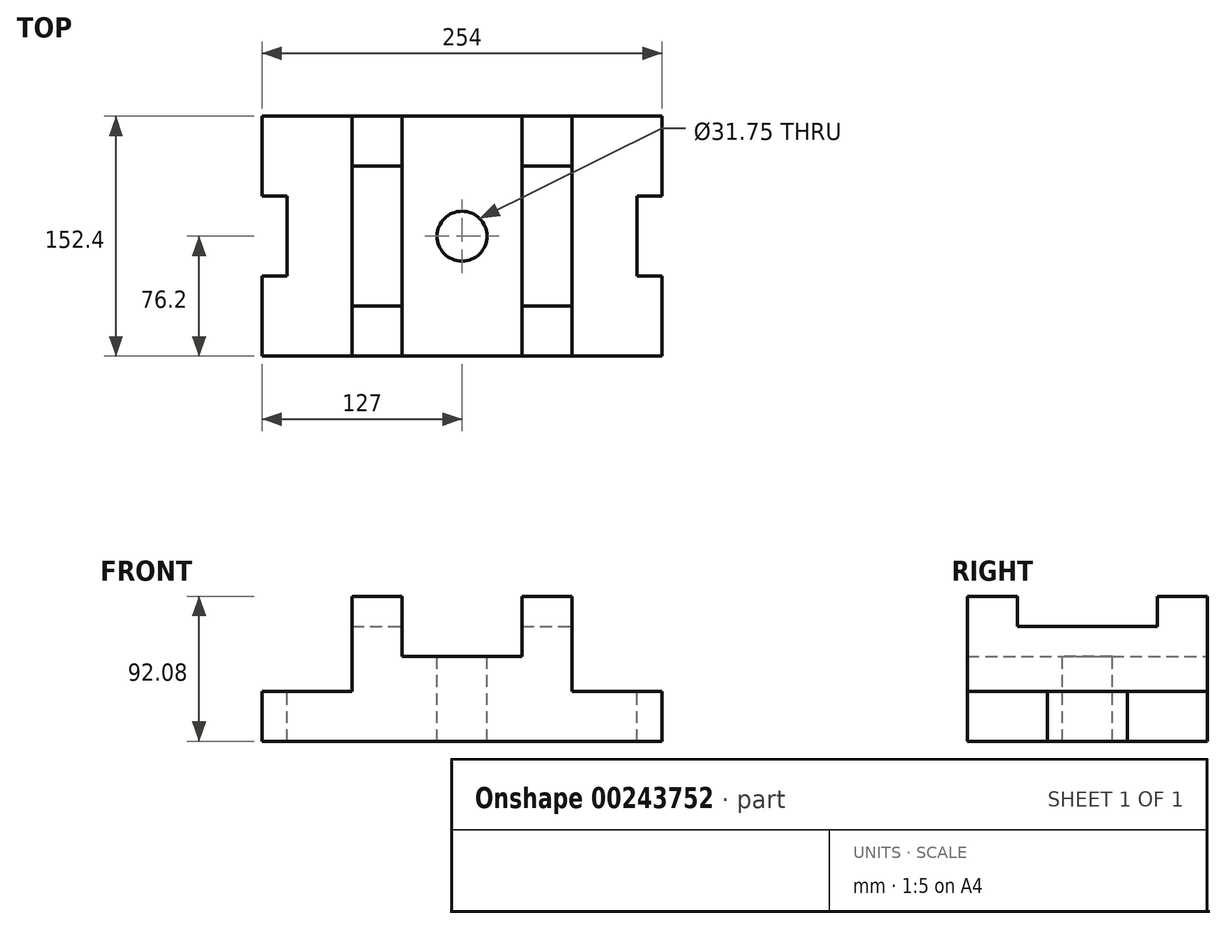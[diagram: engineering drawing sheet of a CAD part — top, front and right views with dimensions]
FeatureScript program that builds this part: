
annotation { "Feature Type Name" : "Feature", "Feature Type Description" : "" }
export const myFeature = defineFeature(function(context is Context, id is Id, definition is map)
    precondition{}
    {
        {
            var Q0;
            Q0=qCreatedBy(makeId("Front.planeOp"),FACE);
            var sketch = newSketch(context, id + "F0", { "sketchPlane" : qUnion([Q0])});
            skLineSegment(sketch, "E0.bottom", {"start": v(0, 0) * mm, "end": v(-254, 0) * mm});
            skLineSegment(sketch, "E0.left", {"start": v(0, 0) * mm, "end": v(0, 31.75) * mm});
            skLineSegment(sketch, "E0.right", {"start": v(-254, 0) * mm, "end": v(-254, 31.75) * mm});
            skLineSegment(sketch, "E1", {"start": v(0, 31.75) * mm, "end": v(-57.15, 31.75) * mm});
            skLineSegment(sketch, "E2", {"start": v(-254, 31.75) * mm, "end": v(-196.85, 31.75) * mm});
            skLineSegment(sketch, "E3", {"start": v(-57.15, 31.75) * mm, "end": v(-57.15, 92.07) * mm});
            skLineSegment(sketch, "E4", {"start": v(-57.15, 92.07) * mm, "end": v(-88.9, 92.07) * mm});
            skLineSegment(sketch, "E5", {"start": v(-88.9, 92.07) * mm, "end": v(-88.9, 73.02) * mm});
            skLineSegment(sketch, "E6", {"start": v(-254, 0) * mm, "end": v(-127, 0) * mm});
            skLineSegment(sketch, "E7.MirrorCS", {"start": v(-165.1, 92.07) * mm, "end": v(-165.1, 73.02) * mm});
            skLineSegment(sketch, "E8.MirrorCS", {"start": v(-196.85, 92.07) * mm, "end": v(-165.1, 92.07) * mm});
            skLineSegment(sketch, "E9.MirrorCS", {"start": v(-196.85, 31.75) * mm, "end": v(-196.85, 92.07) * mm});
            skLineSegment(sketch, "E10", {"start": v(-88.9, 73.02) * mm, "end": v(-165.1, 73.02) * mm});
            skSolve(sketch);
        }
        {
            var Q0;
            Q0=makeQuery(id+"F0.imprint","IMPRINT",FACE,{"disambiguationData":[TD([[makeQuery(id+"F0.imprint","IMPRINT",EDGE,{"derivedFrom":sQuery(id+"F0.wireOp",EDGE,"E0.bottom")}),-1.0]])]});
            extrude(context, id + "F1", {"entities" : qUnion([Q0]), "depth" : 152.4 * mm});
        }
        {
            var Q0;
            Q0=makeQuery(id+"F1.opExtrude","SWEPT_FACE",FACE,{"disambiguationData":[OSD([sQuery(id+"F0.wireOp",EDGE,"E1")])]});
            var sketch = newSketch(context, id + "F2", { "sketchPlane" : qUnion([Q0])});
            skLineSegment(sketch, "E11", {"start": v(0, -152.4) * mm, "end": v(0, -101.6) * mm});
            skLineSegment(sketch, "E12", {"start": v(0, 0) * mm, "end": v(0, -50.8) * mm});
            skLineSegment(sketch, "E13", {"start": v(0, -50.8) * mm, "end": v(-15.87, -50.8) * mm});
            skLineSegment(sketch, "E14", {"start": v(0, -101.6) * mm, "end": v(-15.88, -101.6) * mm});
            skLineSegment(sketch, "E15", {"start": v(-15.87, -50.8) * mm, "end": v(-15.88, -101.6) * mm});
            skSolve(sketch);
        }
        {
            var Q0;
            {var subQ0=sQuery(id+"F2.wireOp",EDGE,"E13");Q0=makeQuery(id+"F2.imprint","IMPRINT",FACE,{"disambiguationData":[TD([[makeQuery(id+"F2.imprint","IMPRINT",EDGE,{"derivedFrom":subQ0}),1.0]])]});}
            extrude(context, id + "F3", {"entities" : qUnion([Q0]), "operationType" : NewBodyOperationType.REMOVE, "endBound" : BoundingType.THROUGH_ALL, "oppositeDirection" : true, "depth" : 25.4 * mm});
        }
        {
            var Q0;
            Q0=makeQuery(id+"F1.opExtrude","SWEPT_FACE",FACE,{"disambiguationData":[OSD([sQuery(id+"F0.wireOp",EDGE,"E2")])]});
            var sketch = newSketch(context, id + "F4", { "sketchPlane" : qUnion([Q0])});
            skLineSegment(sketch, "E16", {"start": v(-254, -152.4) * mm, "end": v(-254, -101.6) * mm});
            skLineSegment(sketch, "E17", {"start": v(-254, -101.6) * mm, "end": v(-254, -50.8) * mm});
            skLineSegment(sketch, "E18", {"start": v(-254, -50.8) * mm, "end": v(-254, 0) * mm});
            skLineSegment(sketch, "E19", {"start": v(-254, -101.6) * mm, "end": v(-238.12, -101.6) * mm});
            skLineSegment(sketch, "E20", {"start": v(-238.12, -101.6) * mm, "end": v(-238.12, -50.8) * mm});
            skLineSegment(sketch, "E21", {"start": v(-254, -50.8) * mm, "end": v(-238.12, -50.8) * mm});
            skLineSegment(sketch, "E22", {"start": v(-254, -50.8) * mm, "end": v(-254, -101.6) * mm});
            skSolve(sketch);
        }
        {
            var Q0;
            Q0=makeQuery(id+"F4.imprint","IMPRINT",FACE,{"disambiguationData":[TD([[makeQuery(id+"F4.imprint","IMPRINT",EDGE,{"derivedFrom":sQuery(id+"F4.wireOp",EDGE,"E19")}),1.0]])]});
            extrude(context, id + "F5", {"entities" : qUnion([Q0]), "operationType" : NewBodyOperationType.REMOVE, "endBound" : BoundingType.THROUGH_ALL, "oppositeDirection" : true, "depth" : 25.4 * mm});
        }
        {
            var Q0;
            Q0=makeQuery(id+"F1.opExtrude","SWEPT_FACE",FACE,{"disambiguationData":[OSD([sQuery(id+"F0.wireOp",EDGE,"E10")])]});
            var sketch = newSketch(context, id + "F6", { "sketchPlane" : qUnion([Q0])});
            skSolve(sketch);
        }
        {
            var Q0;
            {var subQ0=sQuery(id+"F0.wireOp",EDGE,"E10");Q0=makeQuery(id+"F6.imprint","IMPRINT",FACE,{"disambiguationData":[TD([[makeQuery(id+"F6.imprint","IMPRINT",EDGE,{"derivedFrom":makeQuery(id+"F1.opExtrude","CAP_EDGE",EDGE,{"disambiguationData":[OSD([subQ0])],"isStart":true})}),1.0]])]});}
            extrude(context, id + "F7", {"entities" : qUnion([Q0]), "operationType" : NewBodyOperationType.REMOVE, "oppositeDirection" : true, "depth" : 19.05 * mm});
        }
        {
            var Q0;
            Q0=makeQuery(id+"F1.opExtrude","SWEPT_FACE",FACE,{"disambiguationData":[OSD([sQuery(id+"F0.wireOp",EDGE,"E8.MirrorCS")])]});
            var sketch = newSketch(context, id + "F8", { "sketchPlane" : qUnion([Q0])});
            skLineSegment(sketch, "E23.bottom", {"start": v(-196.85, 0) * mm, "end": v(-165.1, 0) * mm});
            skLineSegment(sketch, "E23.top", {"start": v(-196.85, -31.75) * mm, "end": v(-165.1, -31.75) * mm});
            skLineSegment(sketch, "E23.left", {"start": v(-196.85, 0) * mm, "end": v(-196.85, -31.75) * mm});
            skLineSegment(sketch, "E23.right", {"start": v(-165.1, 0) * mm, "end": v(-165.1, -31.75) * mm});
            skLineSegment(sketch, "E24.bottom", {"start": v(-196.85, -152.4) * mm, "end": v(-165.1, -152.4) * mm});
            skLineSegment(sketch, "E24.top", {"start": v(-196.85, -120.65) * mm, "end": v(-165.1, -120.65) * mm});
            skLineSegment(sketch, "E24.left", {"start": v(-196.85, -152.4) * mm, "end": v(-196.85, -120.65) * mm});
            skLineSegment(sketch, "E24.right", {"start": v(-165.1, -152.4) * mm, "end": v(-165.1, -120.65) * mm});
            skLineSegment(sketch, "E25.left", {"start": v(-196.85, -120.65) * mm, "end": v(-196.85, -31.75) * mm});
            skLineSegment(sketch, "E25.right", {"start": v(-165.1, -120.65) * mm, "end": v(-165.1, -31.75) * mm});
            skSolve(sketch);
        }
        {
            var Q0;
            Q0=makeQuery(id+"F1.opExtrude","SWEPT_FACE",FACE,{"disambiguationData":[OSD([sQuery(id+"F0.wireOp",EDGE,"E4")])]});
            var sketch = newSketch(context, id + "F9", { "sketchPlane" : qUnion([Q0])});
            skLineSegment(sketch, "E26.bottom", {"start": v(-88.9, 0) * mm, "end": v(-57.15, 0) * mm});
            skLineSegment(sketch, "E26.top", {"start": v(-88.9, -31.75) * mm, "end": v(-57.15, -31.75) * mm});
            skLineSegment(sketch, "E26.left", {"start": v(-88.9, 0) * mm, "end": v(-88.9, -31.75) * mm});
            skLineSegment(sketch, "E26.right", {"start": v(-57.15, 0) * mm, "end": v(-57.15, -31.75) * mm});
            skLineSegment(sketch, "E27.bottom", {"start": v(-88.9, -152.4) * mm, "end": v(-57.15, -152.4) * mm});
            skLineSegment(sketch, "E27.top", {"start": v(-88.9, -120.65) * mm, "end": v(-57.15, -120.65) * mm});
            skLineSegment(sketch, "E27.left", {"start": v(-88.9, -152.4) * mm, "end": v(-88.9, -120.65) * mm});
            skLineSegment(sketch, "E27.right", {"start": v(-57.15, -152.4) * mm, "end": v(-57.15, -120.65) * mm});
            skLineSegment(sketch, "E28.left", {"start": v(-88.9, -120.65) * mm, "end": v(-88.9, -31.75) * mm});
            skLineSegment(sketch, "E28.right", {"start": v(-57.15, -120.65) * mm, "end": v(-57.15, -31.75) * mm});
            skSolve(sketch);
        }
        {
            var Q0;
            Q0=makeQuery(id+"F9.imprint","IMPRINT",FACE,{"disambiguationData":[TD([[makeQuery(id+"F9.imprint","IMPRINT",EDGE,{"derivedFrom":sQuery(id+"F9.wireOp",EDGE,"E27.top")}),1.0]])]});
            extrude(context, id + "F10", {"entities" : qUnion([Q0]), "operationType" : NewBodyOperationType.REMOVE, "oppositeDirection" : true, "depth" : 19.05 * mm});
        }
        {
            var Q0;
            Q0=makeQuery(id+"F8.imprint","IMPRINT",FACE,{"disambiguationData":[TD([[makeQuery(id+"F8.imprint","IMPRINT",EDGE,{"derivedFrom":sQuery(id+"F8.wireOp",EDGE,"E24.top")}),1.0]])]});
            extrude(context, id + "F11", {"entities" : qUnion([Q0]), "operationType" : NewBodyOperationType.REMOVE, "oppositeDirection" : true, "depth" : 19.05 * mm});
        }
        {
            var Q0;
            Q0=makeQuery(id+"F7.boolean.opBoolean","COPY",FACE,{"derivedFrom":makeQuery(id+"F7.opExtrude","CAP_FACE",FACE,{"disambiguationData":[OSD([sQuery(id+"F0.wireOp",EDGE,"E5"),sQuery(id+"F0.wireOp",EDGE,"E10"),sQuery(id+"F0.wireOp",EDGE,"E7.MirrorCS")])],"isStart":false})});
            var sketch = newSketch(context, id + "F12", { "sketchPlane" : qUnion([Q0])});
            skCircle(sketch, "E29", {"center": v(-127, -76.2) * mm, "radius": 15.88 * mm});
            skSolve(sketch);
        }
        {
            var Q0;
            Q0=makeQuery(id+"F12.imprint","IMPRINT",FACE,{"disambiguationData":[TD([[makeQuery(id+"F12.imprint","IMPRINT",EDGE,{"derivedFrom":sQuery(id+"F12.wireOp",EDGE,"E29")}),1.0]])]});
            extrude(context, id + "F13", {"entities" : qUnion([Q0]), "operationType" : NewBodyOperationType.REMOVE, "endBound" : BoundingType.THROUGH_ALL, "oppositeDirection" : true, "depth" : 25.4 * mm});
        }
    });
